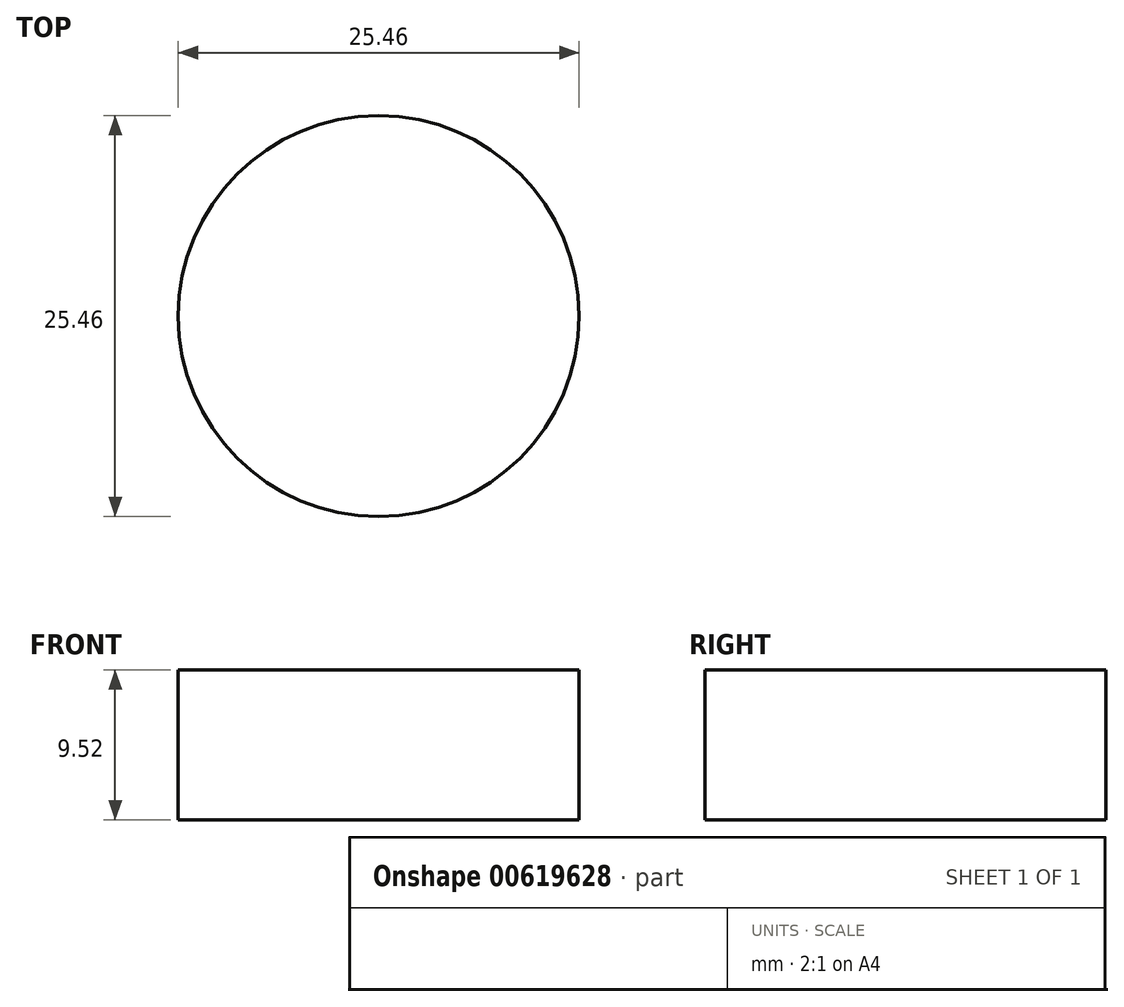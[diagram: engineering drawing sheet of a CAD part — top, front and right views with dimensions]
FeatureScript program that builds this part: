
annotation { "Feature Type Name" : "Feature", "Feature Type Description" : "" }
export const myFeature = defineFeature(function(context is Context, id is Id, definition is map)
    precondition{}
    {
        {
            var Q0;
            Q0=qCreatedBy(makeId("Top.planeOp"),FACE);
            var sketch = newSketch(context, id + "F0", { "sketchPlane" : qUnion([Q0])});
            skCircle(sketch, "E0", {"center": v(0, 0) * mm, "radius": 12.73 * mm});
            skSolve(sketch);
        }
        {
            var Q0;
            Q0=makeQuery(id+"F0.imprint","IMPRINT",FACE,{"disambiguationData":[TD([[makeQuery(id+"F0.imprint","IMPRINT",EDGE,{"derivedFrom":sQuery(id+"F0.wireOp",EDGE,"E0")}),1.0]])]});
            extrude(context, id + "F1", {"entities" : qUnion([Q0]), "endBound" : BoundingType.SYMMETRIC, "depth" : 9.52 * mm, "offsetDistance" : 25.4 * mm});
        }
    });
